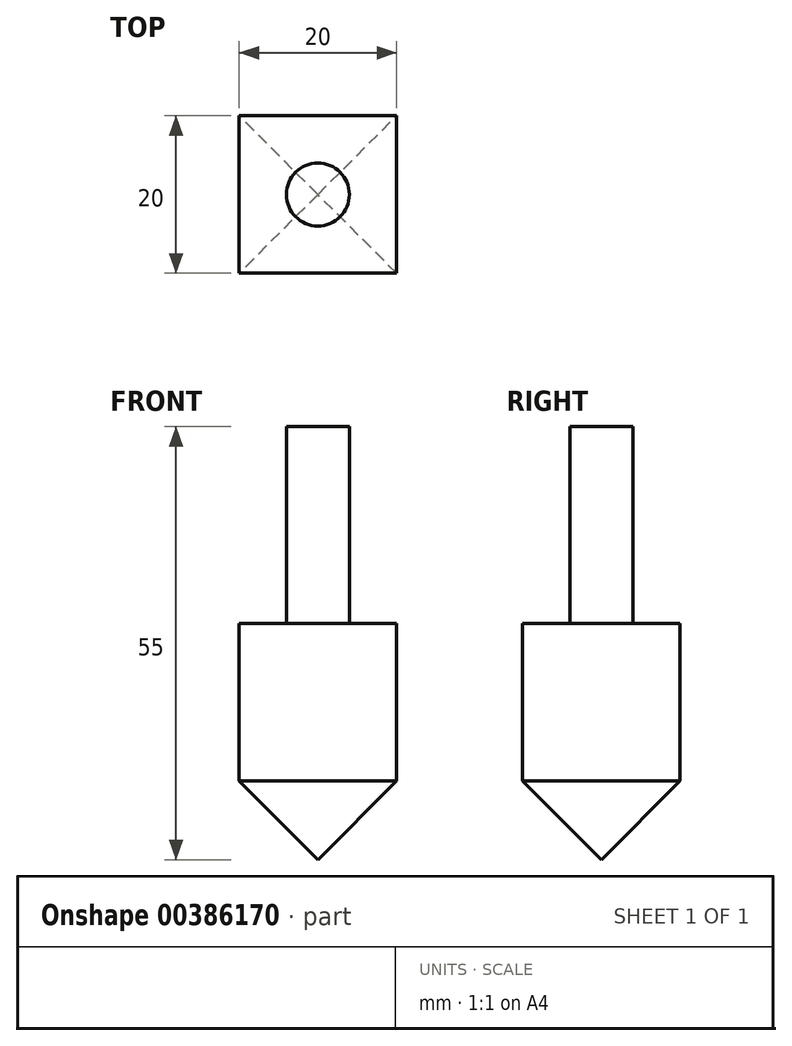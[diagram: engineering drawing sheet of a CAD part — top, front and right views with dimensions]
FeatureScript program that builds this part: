
annotation { "Feature Type Name" : "Feature", "Feature Type Description" : "" }
export const myFeature = defineFeature(function(context is Context, id is Id, definition is map)
    precondition{}
    {
        {
            var Q0;
            Q0=qCreatedBy(makeId("Top.planeOp"),FACE);
            var sketch = newSketch(context, id + "F0", { "sketchPlane" : qUnion([Q0])});
            skLineSegment(sketch, "E0.bottom", {"start": v(10, -10) * mm, "end": v(-10, -10) * mm});
            skLineSegment(sketch, "E0.top", {"start": v(10, 10) * mm, "end": v(-10, 10) * mm});
            skLineSegment(sketch, "E0.left", {"start": v(10, -10) * mm, "end": v(10, 10) * mm});
            skLineSegment(sketch, "E0.right", {"start": v(-10, -10) * mm, "end": v(-10, 10) * mm});
            skPoint(sketch, "E0.middle", {"position": v(0, 0) * mm});
            skSolve(sketch);
        }
        {
            var Q0;
            Q0=makeQuery(id+"F0.imprint","IMPRINT",FACE,{"disambiguationData":[TD([[makeQuery(id+"F0.imprint","IMPRINT",EDGE,{"derivedFrom":sQuery(id+"F0.wireOp",EDGE,"E0.bottom")}),-1.0]])]});
            extrude(context, id + "F1", {"entities" : qUnion([Q0]), "depth" : 30 * mm});
        }
        {
            var Q0;
            Q0=makeQuery(id+"F1.opExtrude","CAP_FACE",FACE,{"disambiguationData":[OSD([sQuery(id+"F0.wireOp",EDGE,"E0.bottom"),sQuery(id+"F0.wireOp",EDGE,"E0.top"),sQuery(id+"F0.wireOp",EDGE,"E0.left"),sQuery(id+"F0.wireOp",EDGE,"E0.right")])],"isStart":false});
            var sketch = newSketch(context, id + "F2", { "sketchPlane" : qUnion([Q0])});
            skCircle(sketch, "E1", {"center": v(0, 0) * mm, "radius": 4 * mm});
            skSolve(sketch);
        }
        {
            var Q0;
            Q0=makeQuery(id+"F2.imprint","IMPRINT",FACE,{"disambiguationData":[TD([[makeQuery(id+"F2.imprint","IMPRINT",EDGE,{"derivedFrom":sQuery(id+"F2.wireOp",EDGE,"E1")}),1.0]])]});
            extrude(context, id + "F3", {"entities" : qUnion([Q0]), "operationType" : NewBodyOperationType.ADD, "depth" : 25 * mm});
        }
        {
            var Q0;
            Q0=makeQuery(id+"F1.opExtrude","CAP_EDGE",EDGE,{"disambiguationData":[OSD([sQuery(id+"F0.wireOp",EDGE,"E0.left")])],"isStart":true});
            var Q1;
            Q1=makeQuery(id+"F1.opExtrude","CAP_EDGE",EDGE,{"disambiguationData":[OSD([sQuery(id+"F0.wireOp",EDGE,"E0.top")])],"isStart":true});
            var Q2;
            Q2=makeQuery(id+"F1.opExtrude","CAP_EDGE",EDGE,{"disambiguationData":[OSD([sQuery(id+"F0.wireOp",EDGE,"E0.right")])],"isStart":true});
            var Q3;
            Q3=makeQuery(id+"F1.opExtrude","CAP_EDGE",EDGE,{"disambiguationData":[OSD([sQuery(id+"F0.wireOp",EDGE,"E0.bottom")])],"isStart":true});
            chamfer(context, id + "F4", {"entities" : qUnion([Q0, Q1, Q2, Q3]), "width" : 10 * mm, "tangentPropagation" : true});
        }
    });
